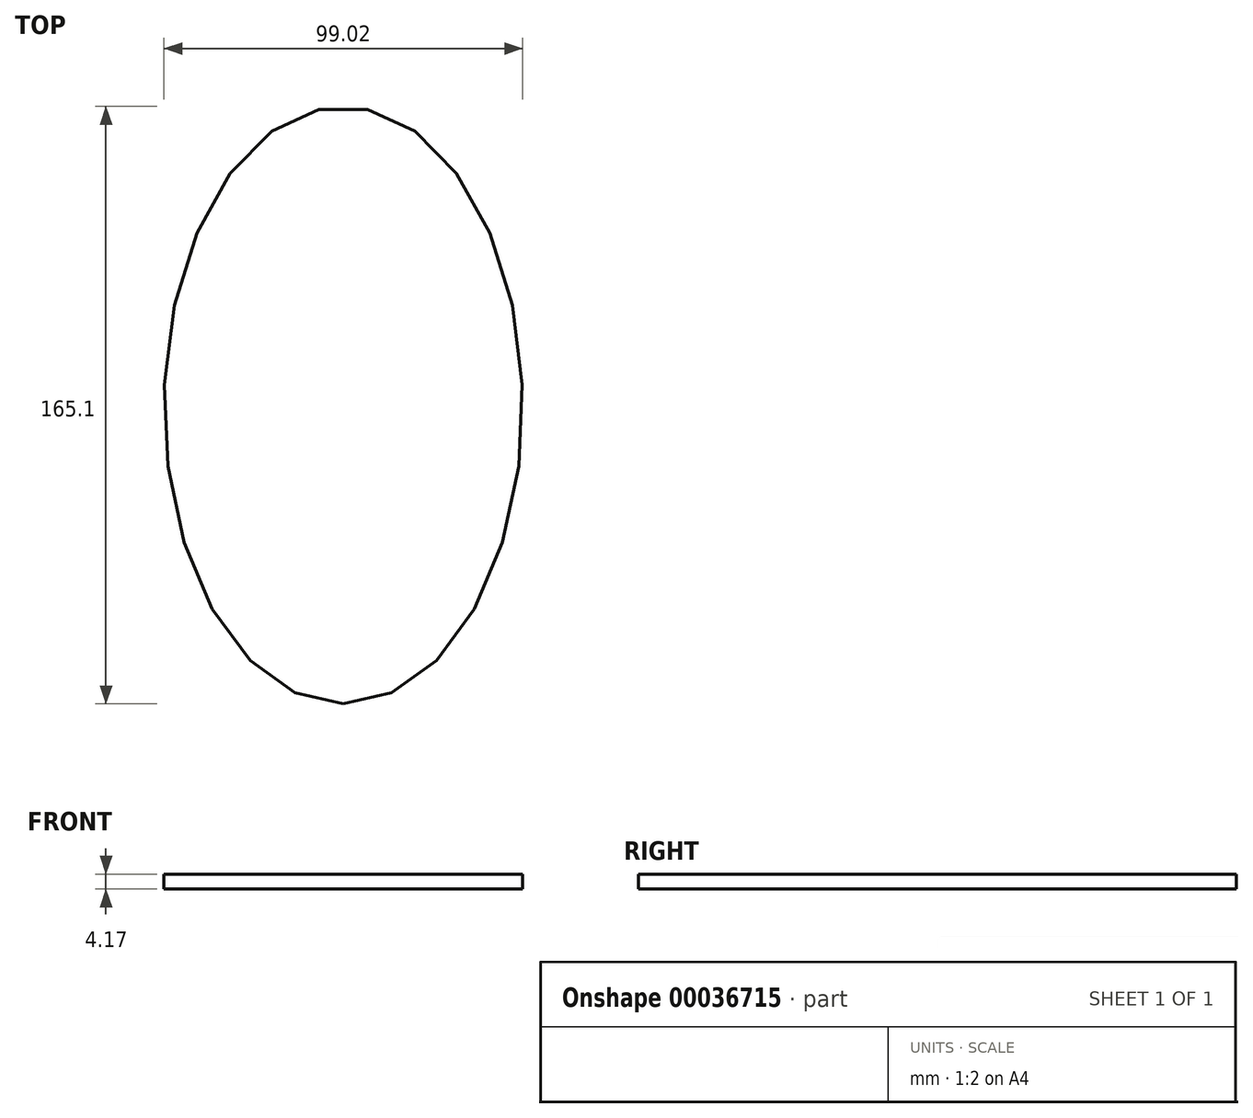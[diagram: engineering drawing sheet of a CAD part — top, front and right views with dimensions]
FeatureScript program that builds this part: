
annotation { "Feature Type Name" : "Feature", "Feature Type Description" : "" }
export const myFeature = defineFeature(function(context is Context, id is Id, definition is map)
    precondition{}
    {
        {
            var Q0;
            Q0=qCreatedBy(makeId("Top.planeOp"),FACE);
            var sketch = newSketch(context, id + "F0", { "sketchPlane" : qUnion([Q0])});
            skEllipse(sketch, "E0", {"center": v(0, 0) * mm, "majorRadius": 82.55 * mm, "minorRadius": 49.51 * mm, "majorAxis": v(0, -1)});
            skSolve(sketch);
        }
        {
            var Q0;
            Q0=makeQuery(id+"F0.imprint","IMPRINT",FACE,{"disambiguationData":[TD([[makeQuery(id+"F0.imprint","IMPRINT",EDGE,{"derivedFrom":sQuery(id+"F0.wireOp",EDGE,"E0")}),1.0]])]});
            extrude(context, id + "F1", {"entities" : qUnion([Q0]), "depth" : 4.17 * mm});
        }
    });
